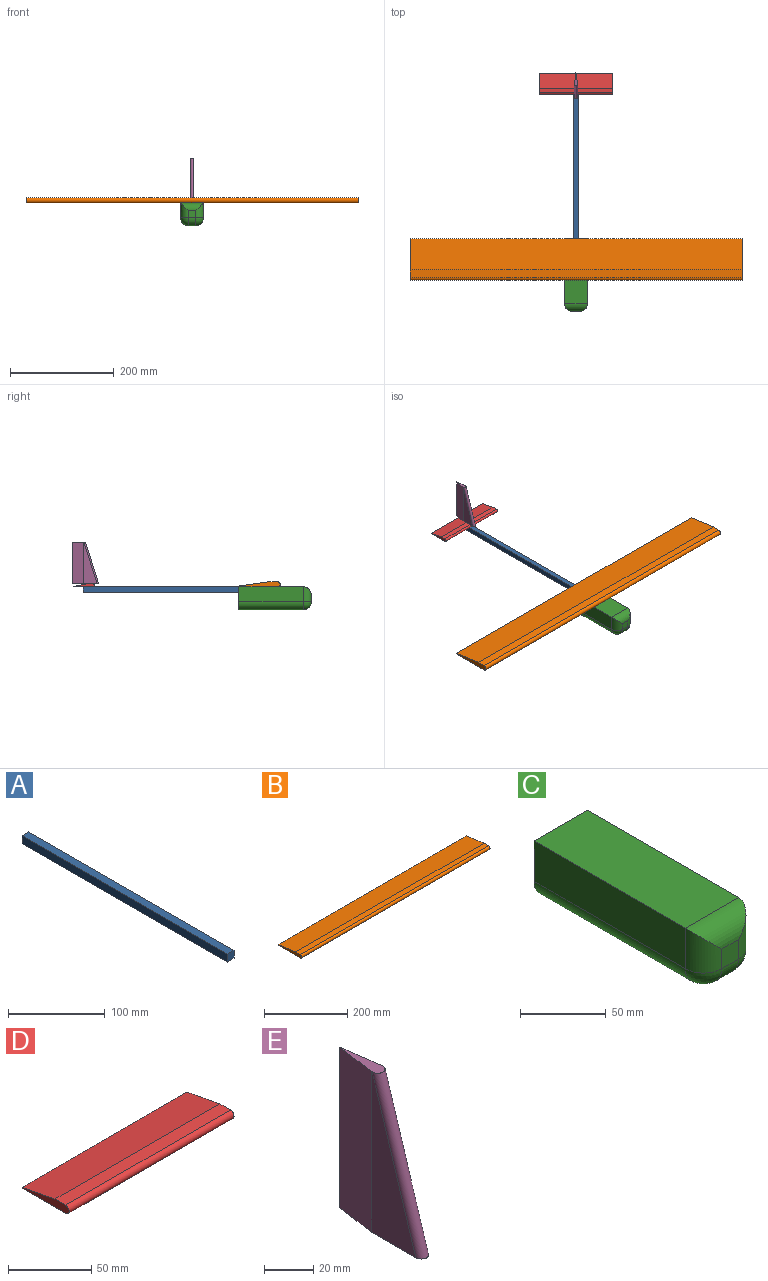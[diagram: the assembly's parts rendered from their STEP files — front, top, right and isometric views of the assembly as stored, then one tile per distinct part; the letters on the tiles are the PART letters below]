
ASSEMBLY  parts=5 mates=4
PART A: 6 faces, bbox 10x300x10 mm
  f0: plane 10x10mm, normal (0,1,0), area 100mm2, adj f1,f3,f4,f5
  f1: plane 300x10mm, normal (-1,0,0), area 3000mm2, adj f0,f2,f4,f5
  f2: plane 10x10mm, normal (0,-1,0), area 100mm2, adj f1,f3,f4,f5
  f3: plane 300x10mm, normal (1,0,0), area 3000mm2, adj f0,f2,f4,f5
  f4: plane 300x10mm, normal (0,0,1), area 3000mm2, adj f0,f1,f2,f3
  f5: plane 300x10mm, normal (0,0,-1), area 3000mm2, adj f0,f1,f2,f3
PART B: 7 faces, bbox 640x80x10 mm
  f0: plane 80x10mm, normal (1,0,0), area 536.3mm2, adj f1,f3,f4,f5,f6
  f1: plane 640x1.57mm, normal (0,1,0), area 1003.2mm2, adj f0,f2,f4,f5
  f2: plane 80x10mm, normal (-1,0,0), area 536.3mm2, adj f1,f3,f4,f5,f6
  f3: plane 640x15mm, normal (0,0,1), area 9600mm2, adj f0,f2,f5,f6
  f4: plane 640x75mm, normal (0,0,-1), area 48000mm2, adj f0,f1,f2,f6
  f5: plane 640x60mm, normal (0,0.14,0.99), area 38777.4mm2, adj f0,f1,f2,f3
  f6: cylinder r=5mm len=640mm, axis (-1,0,0), area 10053.1mm2, adj f0,f2,f3,f4
PART C: 14 faces, bbox 44x140x44 mm
  f0: plane 125x29mm, normal (1,0,0), area 3625mm2, adj f1,f4,f6,f8
  f1: plane 44x44mm, normal (0,1,0), area 1839.4mm2, adj f0,f2,f4,f5,f6,f10
  f2: plane 125x29mm, normal (-1,0,0), area 3625mm2, adj f1,f4,f10,f13
  f3: plane 14x14mm, normal (0,-1,0), area 196mm2, adj f8,f9,f11,f13
  f4: plane 125x44mm, normal (0,0,1), area 5500mm2, adj f0,f1,f2,f11
  f5: plane 125x14mm, normal (0,0,-1), area 1750mm2, adj f1,f6,f9,f10
  f6: cylinder r=15mm len=125mm, axis (0,1,0), area 2945.2mm2, adj f0,f1,f5,f7
  f7: sphere r=15mm, area 353.4mm2, adj f6,f8,f9
  f8: cylinder r=15mm len=29mm, axis (0,0,-1), area 554.9mm2, adj f0,f3,f7,f11
  f9: cylinder r=15mm len=15mm, axis (1,0,0), area 329.9mm2, adj f3,f5,f7,f12
  f10: cylinder r=15mm len=125mm, axis (0,-1,0), area 2945.2mm2, adj f1,f2,f5,f12
  f11: cylinder r=15mm len=44mm, axis (-1,0,0), area 779.9mm2, adj f3,f4,f8,f13
  f12: sphere r=15mm, area 353.4mm2, adj f9,f10,f13
  f13: cylinder r=15mm len=29mm, axis (0,0,1), area 554.9mm2, adj f2,f3,f11,f12
PART D: 7 faces, bbox 140x40x6 mm
  f0: plane 40x6mm, normal (1,0,0), area 159.9mm2, adj f1,f3,f4,f5,f6
  f1: plane 140x0.56mm, normal (0,1,0), area 78mm2, adj f0,f2,f4,f6
  f2: plane 40x6mm, normal (-1,0,0), area 159.9mm2, adj f1,f3,f4,f5,f6
  f3: plane 140x9mm, normal (0,0,1), area 1260mm2, adj f0,f2,f5,f6
  f4: plane 140x37mm, normal (0,0,-1), area 5180mm2, adj f0,f1,f2,f5
  f5: cylinder r=3mm len=140mm, axis (-1,0,0), area 1319.5mm2, adj f0,f2,f3,f4
  f6: plane 140x28mm, normal (0,0.19,0.98), area 3993.4mm2, adj f0,f1,f2,f3
PART E: 7 faces, bbox 6x50x81.8 mm
  f0: plane 50x6mm, normal (0,0,-1), area 231.9mm2, adj f2,f3,f4,f5,f6
  f1: plane 25x6mm, normal (0,0,1), area 81.9mm2, adj f2,f3,f4,f5,f6
  f2: plane 80x25.51mm, normal (1,0,0), area 1040.9mm2, adj f0,f1,f4,f5
  f3: plane 80x25.51mm, normal (-1,0,0), area 1040.9mm2, adj f0,f1,f4,f6
  f4: cylinder r=3mm len=81.79mm, axis (0,0.3,0.95), area 789.9mm2, adj f0,f1,f2,f3
  f5: plane 80x21.35mm, normal (0.99,0.14,0), area 1724.5mm2, adj f0,f1,f2,f6
  f6: plane 80x21.35mm, normal (-0.99,0.14,0), area 1724.5mm2, adj f0,f1,f3,f5
PLACE A t=(-25.29,211,20.4)mm
PLACE B t=(-25.29,21,30.4)mm
PLACE C t=(-25.29,-9,-13.6)mm
PLACE D t=(-25.29,359.5,30.4)mm
PLACE E t=(-25.29,356.01,76.4)mm
MATE fastened B.f1 <-> C.f1  axis (0,1,0) through (-25.29,61,30.4)mm
MATE fastened D.f4 <-> A.f4  axis (0,0,-1) through (-25.29,361,30.4)mm
MATE fastened E.f0 <-> D.f3  axis (0,0,-1) through (-25.29,351.5,36.4)mm
MATE fastened A.f2 <-> C.f1  axis (0,-1,0) through (-25.29,61,30.4)mm
